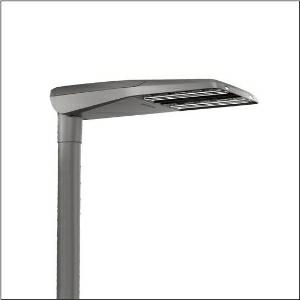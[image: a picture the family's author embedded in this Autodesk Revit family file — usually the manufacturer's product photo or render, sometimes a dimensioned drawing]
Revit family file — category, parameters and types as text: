
# Revit family: streetlight_sl_11_iq_midi___st1_2a_5xc3a41f08me_055e
name_source: partatom
category: Lighting Fixtures
units: mm (PartAtom-declared; Revit-internal decimal feet)

## family parameters
Cut with Voids When Loaded = No
Host = Face
Light Source = No
Part Type = Normal
Room Calculation Point = No
Round Connector Dimension = Use Diameter
Shared = No

## types (1)
- --- (1 x LED, 18900 lm, 124.7 W, 4000K)
    Apparent Load = 125 VA
    CIE Flux Codes = 32 70 96 100 100
    Color Rendering = 70
    Color Temperature = 4000K
    Default Elevation = 1800 mm
    Description = Streetlight SL 11 iQ midi, mast luminaire, primary light control with 3 zone facetted reflector, of plastic, silver coated, highly specular, primary optical cover: cover, of PMMA, transparent, light distribution: ST1.2a, light emission: direct distribution, primary light characteristic: asymmetric, installation type: post-top, side-entry, lamps: LED, High Power LED, rated values: 18.900lm | 124,7W | 151,6lm/W (begin service life); end service life: 18.900lm | 132,2W; at 50% lumin. flux: 9.450lm | 57,4W | 164,6lm/W, colour temperature: 4000K, colour rendering: CRI > 70, light colour: 740, light setting 1 begin service life: 100% | 18.900lm | 124,7W | 151,6lm/W | 4.000K, light setting 1 end service life: 132,2W, further light settings possible, control: Street-Remote, optimised constant luminous flux control (CLO 2.0), Desk-Remote (wireless, voltage-free reading and setting of iQ features in the workshop via application-optimized NFC function/RFID function), Light-Fading, Smart-Wire, Night-Set, Lumen-Switch, Temp-Guard, Auto-Match, with cable H07RN-F 5x 1.5mm², mains connection: 230..240V, AC, 50/60Hz, connection cable pre-assembled, cable length: 12,5m, luminaire housing, of diecast aluminium, powder-coated, Siteco® metallic grey (DB 702S), please order mast flange separately, inclination adjustable without tools: 0°, 5°, 10°, 15° (post-top) | 0°, -5°, -10°, -15° (side-entry), sealing non-destructively replaceable, multi-level sealing system, length: 780mm, width: 376mm, height: 118mm, mast flange for spigot size: 42mm (side-entry): 5XC10008XM4, 60/48mm (side-entry/post-top): 5XC10108XM2, 76/60mm (side-entry/post-top): 5XC10108XM1, equipment: Power, protection rating (complete): IP66, insulation class (complete): insulation class II (safety insulation), certification: CE, ENEC, ENEC+, VDE, impact resistance: IK10, permissible operating ambient temperature for outdoor applications: -25..+50°C, standard-compliant lighting for roads and squares, Environmental Product Declaration (EPD) tested and certified by an independent institute, packaging unit: 1 piece

Light Distribution: ST1.2a
    Height = 118 mm
    Lamp = 1 x LED
    Lamp Light Flux = 18900 lm
    Lamp Power = 124.7 W
    Lamp count = 1
    Length = 780 mm
    Luminous efficacy = 152 lm/W
    Manufacturer = Siteco
    ModVariant = No
    Model = 5XC3A41F08ME
    Number of Poles = 1
    OnlyDefault = Yes
    Power Factor = 1
    Product Name = Streetlight SL 11 iQ midi | ST1.2a
    Product group = mast luminaire | pylon top
    ProductGroupID = 6100
    Protection Class = Protection class II
    Protection Degree = IP 66
    RLX_Detail_Level = 1
    RLX_Emergency_Light_Flux = 0 lm
    RLX_Emergency_Type = 0
    RLX_Emergency_Type_DB = No
    RlxData = <blob elided: 70953 chars, md5=14cc7937>
    Socket = socket
    Standby Power = 0 W
    System Light Flux = 18900 lm
    System Power = 125 W
    Type Comments = factory setting: luminous flux: 100 % | dim-lin: 254 | 557 mA
    Type Image = l_1005960.jpg
    URL = http://relux.com
    VarID = @adj_196296
    Voltage = 0 V
    Weight = 0.00 kg
    Width = 376 mm

## geometry (parser evidence)
native form markers: Blend x4, Sweep x13
no freeform markers — native parametric forms only
